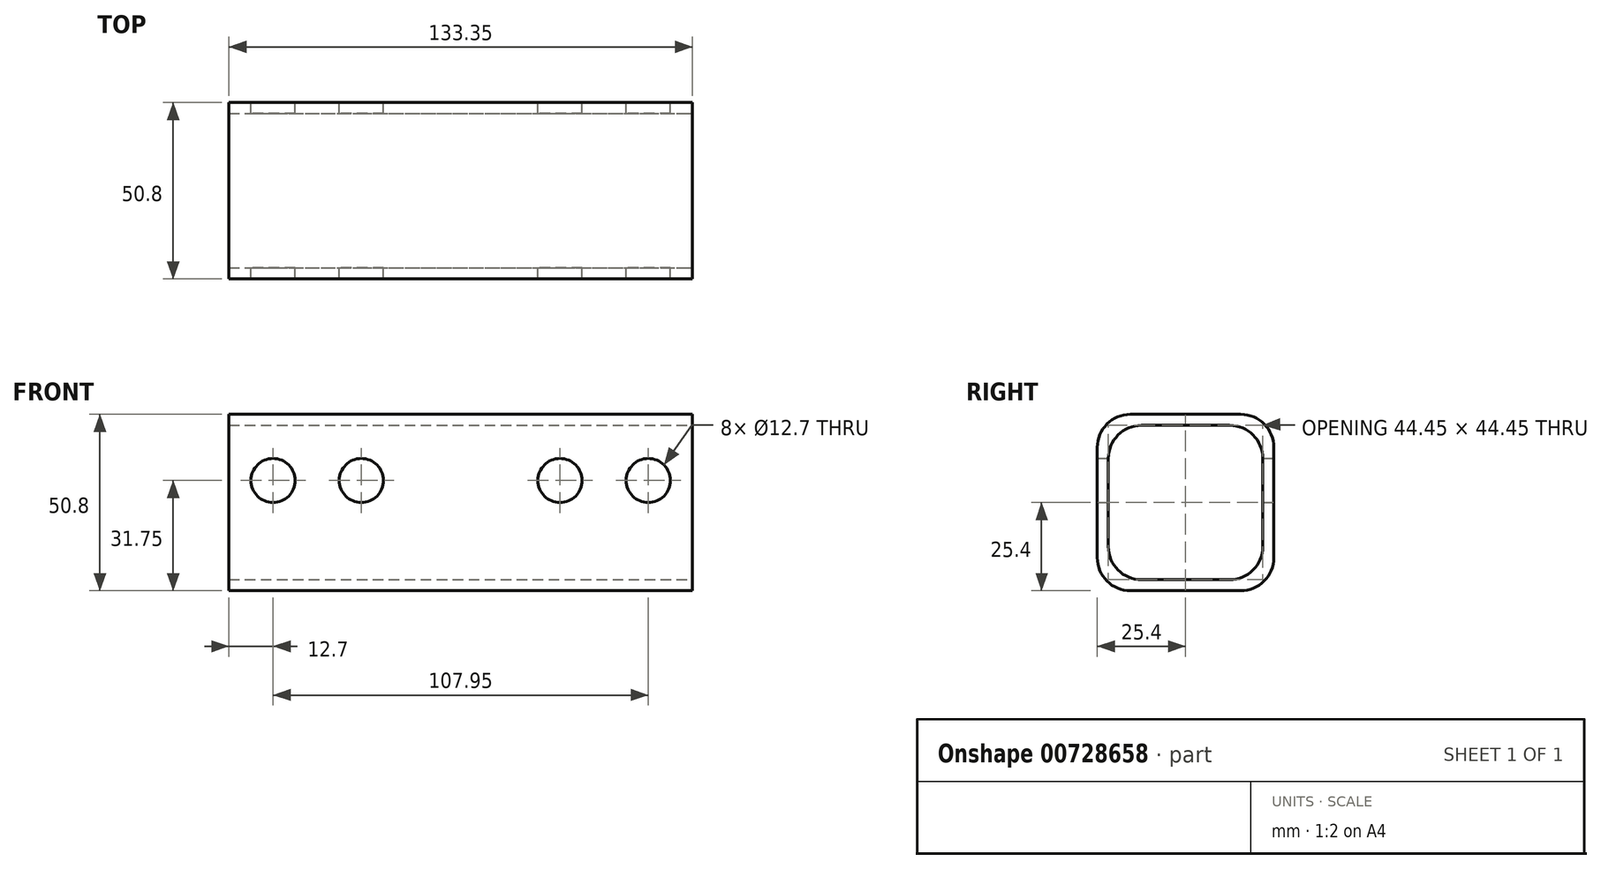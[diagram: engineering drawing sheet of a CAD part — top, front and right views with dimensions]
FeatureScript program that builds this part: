
annotation { "Feature Type Name" : "Feature", "Feature Type Description" : "" }
export const myFeature = defineFeature(function(context is Context, id is Id, definition is map)
    precondition{}
    {
        {
            var Q0;
            Q0=qCreatedBy(makeId("Right.planeOp"),FACE);
            var sketch = newSketch(context, id + "F0", { "sketchPlane" : qUnion([Q0])});
            skLineSegment(sketch, "E0.bottom", {"start": v(0, 0) * mm, "end": v(50.8, 0) * mm});
            skLineSegment(sketch, "E0.top", {"start": v(0, 50.8) * mm, "end": v(50.8, 50.8) * mm});
            skLineSegment(sketch, "E0.left", {"start": v(0, 0) * mm, "end": v(0, 50.8) * mm});
            skLineSegment(sketch, "E0.right", {"start": v(50.8, 0) * mm, "end": v(50.8, 50.8) * mm});
            skSolve(sketch);
        }
        {
            var Q0;
            Q0=qSketchRegion(id+"F0",true);
            extrude(context, id + "F1", {"entities" : qUnion([Q0]), "oppositeDirection" : true, "depth" : 133.35 * mm, "offsetDistance" : 25.4 * mm});
        }
        {
            var Q0;
            Q0=makeQuery(id+"F1.opExtrude","CAP_FACE",FACE,{"disambiguationData":[OSD([sQuery(id+"F0.wireOp",EDGE,"E0.bottom"),sQuery(id+"F0.wireOp",EDGE,"E0.top"),sQuery(id+"F0.wireOp",EDGE,"E0.left"),sQuery(id+"F0.wireOp",EDGE,"E0.right")])],"isStart":true});
            var sketch = newSketch(context, id + "F2", { "sketchPlane" : qUnion([Q0])});
            skLineSegment(sketch, "E1.0", {"start": v(3.17, 47.63) * mm, "end": v(47.63, 47.63) * mm});
            skLineSegment(sketch, "E1.1", {"start": v(3.17, 3.17) * mm, "end": v(3.17, 47.63) * mm});
            skLineSegment(sketch, "E1.2", {"start": v(3.17, 3.17) * mm, "end": v(47.63, 3.17) * mm});
            skLineSegment(sketch, "E1.3", {"start": v(47.63, 3.17) * mm, "end": v(47.63, 47.63) * mm});
            skSolve(sketch);
        }
        {
            var Q0;
            Q0=qSketchRegion(id+"F2",true);
            extrude(context, id + "F3", {"entities" : qUnion([Q0]), "operationType" : NewBodyOperationType.REMOVE, "oppositeDirection" : true, "depth" : 876.3 * mm, "offsetDistance" : 25.4 * mm});
        }
        {
            var Q0;
            Q0=makeQuery(id+"F3.boolean.opBoolean","COPY",EDGE,{"derivedFrom":makeQuery(id+"F3.opExtrude","SWEPT_EDGE",EDGE,{"disambiguationData":[OSD([sQuery(id+"F2.wireOp",EDGE,"E1.1"),sQuery(id+"F2.wireOp",EDGE,"E1.2")])]})});
            var Q1;
            Q1=makeQuery(id+"F3.boolean.opBoolean","COPY",EDGE,{"derivedFrom":makeQuery(id+"F3.opExtrude","SWEPT_EDGE",EDGE,{"disambiguationData":[OSD([sQuery(id+"F2.wireOp",EDGE,"E1.2"),sQuery(id+"F2.wireOp",EDGE,"E1.3")])]})});
            var Q2;
            Q2=makeQuery(id+"F3.boolean.opBoolean","COPY",EDGE,{"derivedFrom":makeQuery(id+"F3.opExtrude","SWEPT_EDGE",EDGE,{"disambiguationData":[OSD([sQuery(id+"F2.wireOp",EDGE,"E1.0"),sQuery(id+"F2.wireOp",EDGE,"E1.3")])]})});
            var Q3;
            Q3=makeQuery(id+"F3.boolean.opBoolean","COPY",EDGE,{"derivedFrom":makeQuery(id+"F3.opExtrude","SWEPT_EDGE",EDGE,{"disambiguationData":[OSD([sQuery(id+"F2.wireOp",EDGE,"E1.0"),sQuery(id+"F2.wireOp",EDGE,"E1.1")])]})});
            var Q4;
            Q4=makeQuery(id+"F1.opExtrude","SWEPT_EDGE",EDGE,{"disambiguationData":[OSD([sQuery(id+"F0.wireOp",EDGE,"E0.bottom"),sQuery(id+"F0.wireOp",EDGE,"E0.right")])]});
            var Q5;
            Q5=makeQuery(id+"F1.opExtrude","SWEPT_EDGE",EDGE,{"disambiguationData":[OSD([sQuery(id+"F0.wireOp",EDGE,"E0.top"),sQuery(id+"F0.wireOp",EDGE,"E0.right")])]});
            var Q6;
            Q6=makeQuery(id+"F1.opExtrude","SWEPT_EDGE",EDGE,{"disambiguationData":[OSD([sQuery(id+"F0.wireOp",EDGE,"E0.top"),sQuery(id+"F0.wireOp",EDGE,"E0.left")])]});
            var Q7;
            Q7=makeQuery(id+"F1.opExtrude","SWEPT_EDGE",EDGE,{"disambiguationData":[OSD([sQuery(id+"F0.wireOp",EDGE,"E0.bottom"),sQuery(id+"F0.wireOp",EDGE,"E0.left")])]});
            fillet(context, id + "F4", {"entities" : qUnion([Q0, Q1, Q2, Q3, Q4, Q5, Q6, Q7]), "radius" : 9.52 * mm, "tangentPropagation" : true, "allowEdgeOverflow" : false});
        }
        {
            var Q0;
            Q0=makeQuery(id+"F1.opExtrude","SWEPT_FACE",FACE,{"disambiguationData":[OSD([sQuery(id+"F0.wireOp",EDGE,"E0.right")])]});
            var sketch = newSketch(context, id + "F5", { "sketchPlane" : qUnion([Q0])});
            skLineSegment(sketch, "E2", {"start": v(120.65, 31.75) * mm, "end": v(95.25, 31.75) * mm});
            skLineSegment(sketch, "E3", {"start": v(38.1, 31.75) * mm, "end": v(12.7, 31.75) * mm});
            skSolve(sketch);
        }
        {
            var Q0;
            Q0=sQuery(id+"F5.wireOp",VERTEX,"E2.start");
            var Q1;
            Q1=sQuery(id+"F5.wireOp",VERTEX,"E2.end");
            var Q2;
            Q2=sQuery(id+"F5.wireOp",VERTEX,"E3.start");
            var Q3;
            Q3=sQuery(id+"F5.wireOp",VERTEX,"E3.end");
            var Q4;
            Q4=makeQuery(id+"F1.opExtrude","SWEPT_BODY",BODY,{"disambiguationData":[OSD([sQuery(id+"F0.wireOp",EDGE,"E0.bottom"),sQuery(id+"F0.wireOp",EDGE,"E0.top"),sQuery(id+"F0.wireOp",EDGE,"E0.left"),sQuery(id+"F0.wireOp",EDGE,"E0.right")])]});
            hole(context, id + "F6", {"style" : HoleStyle.SIMPLE, "endStyle" : HoleEndStyle.BLIND, "holeDiameter" : 12.7 * mm, "majorDiameter" : 6.35 * mm, "holeDepth" : 127 * mm, "isTappedThrough" : true, "tappedDepth" : 12.7 * mm, "tapClearance" : 3, "locations" : qUnion([Q0, Q1, Q2, Q3]), "scope" : qUnion([Q4])});
        }
    });
